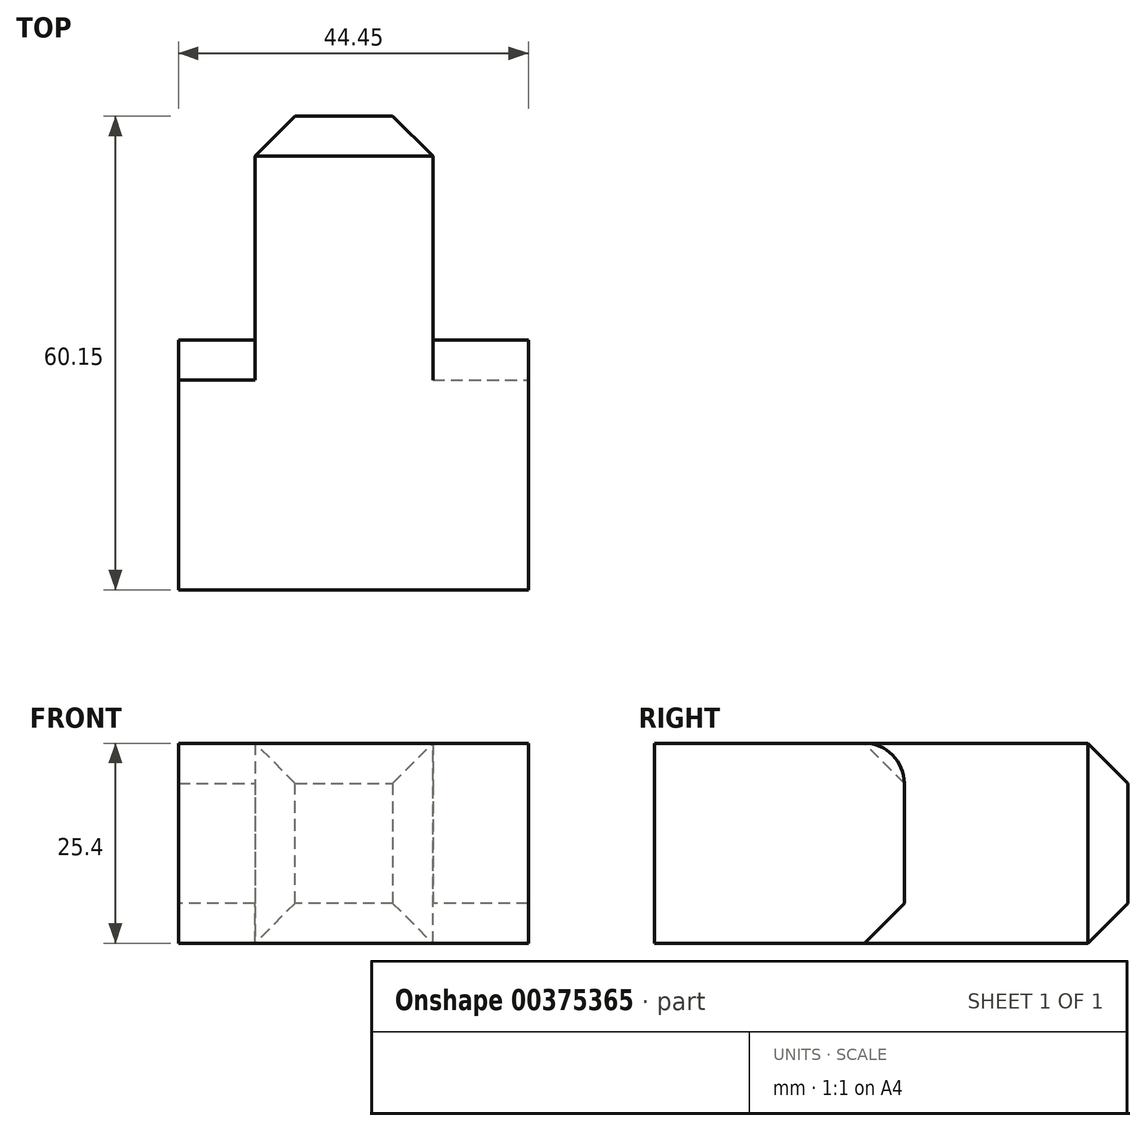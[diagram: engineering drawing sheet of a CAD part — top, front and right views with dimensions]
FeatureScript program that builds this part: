
annotation { "Feature Type Name" : "Feature", "Feature Type Description" : "" }
export const myFeature = defineFeature(function(context is Context, id is Id, definition is map)
    precondition{}
    {
        {
            var Q0;
            Q0=qCreatedBy(makeId("Top.planeOp"),FACE);
            var sketch = newSketch(context, id + "F0", { "sketchPlane" : qUnion([Q0])});
            skLineSegment(sketch, "E0", {"start": v(0, 0) * mm, "end": v(44.45, 0) * mm});
            skLineSegment(sketch, "E1", {"start": v(0, 0) * mm, "end": v(0, 31.75) * mm});
            skLineSegment(sketch, "E2", {"start": v(0, 31.75) * mm, "end": v(9.73, 31.75) * mm});
            skLineSegment(sketch, "E3", {"start": v(9.73, 31.75) * mm, "end": v(9.73, 60.15) * mm});
            skLineSegment(sketch, "E4", {"start": v(9.73, 60.15) * mm, "end": v(21.02, 60.15) * mm});
            skLineSegment(sketch, "E5", {"start": v(44.45, 0) * mm, "end": v(44.45, 31.75) * mm});
            skLineSegment(sketch, "E6", {"start": v(44.45, 31.75) * mm, "end": v(32.32, 31.75) * mm});
            skLineSegment(sketch, "E7", {"start": v(32.32, 31.75) * mm, "end": v(32.32, 60.15) * mm});
            skLineSegment(sketch, "E8", {"start": v(21.02, 60.15) * mm, "end": v(32.32, 60.15) * mm});
            skSolve(sketch);
        }
        {
            var Q0;
            Q0 = qSketchRegion(id + "F0", true);
            extrude(context, id + "F1", {"entities" : qUnion([Q0]), "depth" : 25.4 * mm});
        }
        {
            var Q0;
            Q0=makeQuery(id+"F1.opExtrude","CAP_EDGE",EDGE,{"disambiguationData":[OSD([sQuery(id+"F0.wireOp",EDGE,"E2")])],"isStart":false});
            chamfer(context, id + "F2", {"entities" : qUnion([Q0]), "width" : 5.08 * mm, "tangentPropagation" : true});
        }
        {
            var Q0;
            Q0=makeQuery(id+"F1.opExtrude","CAP_EDGE",EDGE,{"disambiguationData":[OSD([sQuery(id+"F0.wireOp",EDGE,"E2")])],"isStart":true});
            chamfer(context, id + "F3", {"entities" : qUnion([Q0]), "width" : 5.08 * mm, "tangentPropagation" : true});
        }
        {
            var Q0;
            Q0=makeQuery(id+"F1.opExtrude","CAP_EDGE",EDGE,{"disambiguationData":[OSD([sQuery(id+"F0.wireOp",EDGE,"E6")])],"isStart":false});
            fillet(context, id + "F4", {"entities" : qUnion([Q0]), "radius" : 5.08 * mm, "tangentPropagation" : true, "allowEdgeOverflow" : false});
        }
        {
            var Q0;
            Q0=makeQuery(id+"F1.opExtrude","CAP_EDGE",EDGE,{"disambiguationData":[OSD([sQuery(id+"F0.wireOp",EDGE,"E6")])],"isStart":true});
            chamfer(context, id + "F5", {"entities" : qUnion([Q0]), "width" : 5.08 * mm, "tangentPropagation" : true});
        }
        {
            var Q0;
            Q0=makeQuery(id+"F1.opExtrude","SWEPT_FACE",FACE,{"disambiguationData":[OSD([sQuery(id+"F0.wireOp",EDGE,"E4"),sQuery(id+"F0.wireOp",EDGE,"E8")])]});
            chamfer(context, id + "F6", {"entities" : qUnion([Q0]), "width" : 5.08 * mm, "tangentPropagation" : true});
        }
    });
